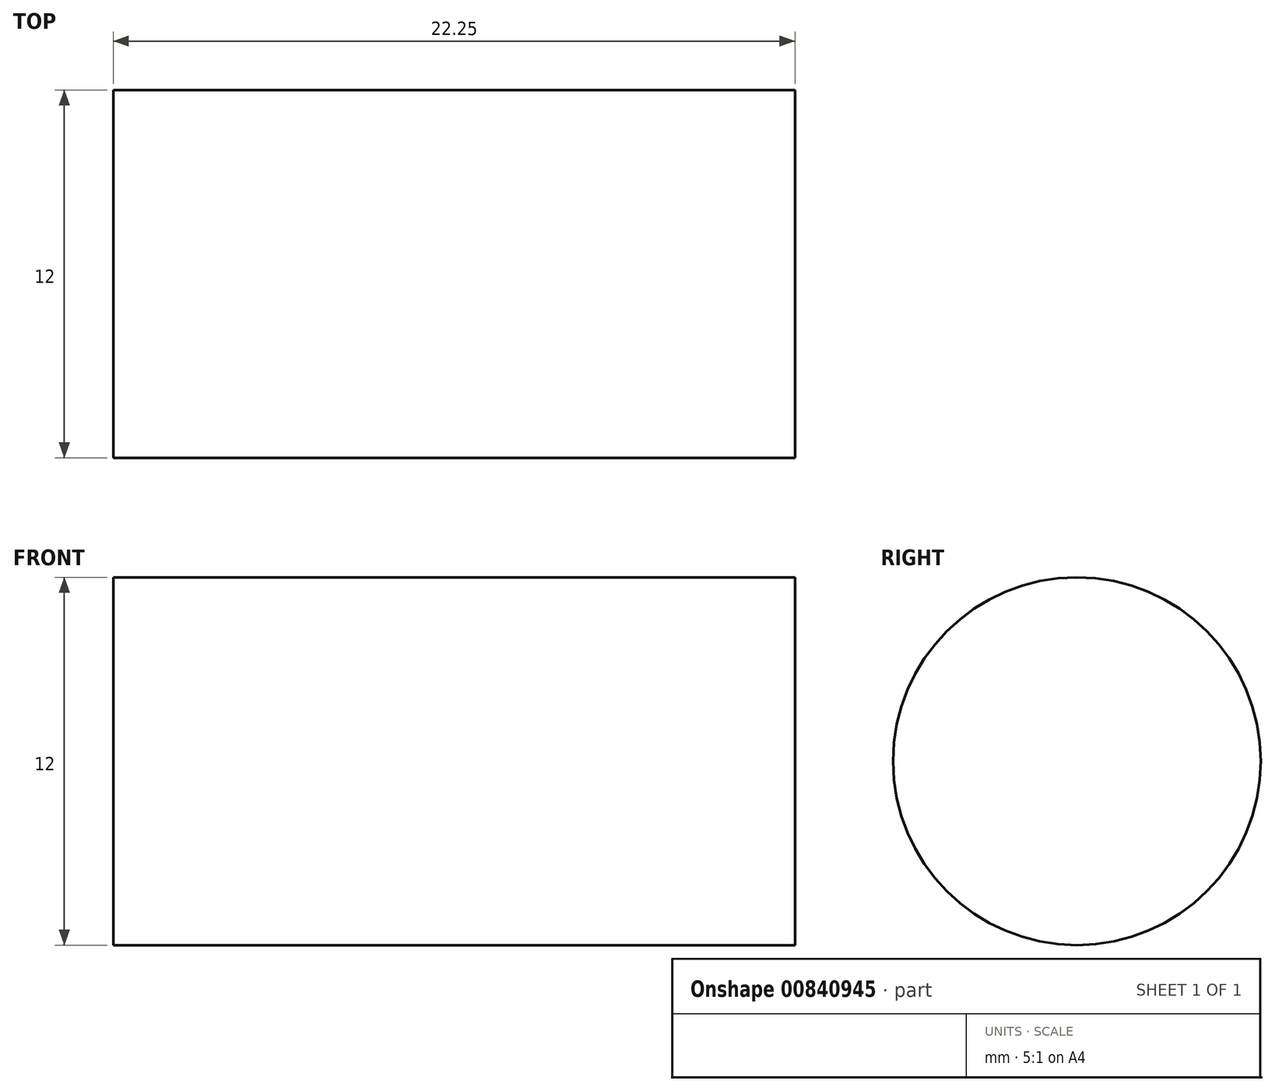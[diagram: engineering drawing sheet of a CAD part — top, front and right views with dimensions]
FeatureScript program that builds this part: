
annotation { "Feature Type Name" : "Feature", "Feature Type Description" : "" }
export const myFeature = defineFeature(function(context is Context, id is Id, definition is map)
    precondition{}
    {
        {
            var Q0;
            Q0=qCreatedBy(makeId("Right.planeOp"),FACE);
            var sketch = newSketch(context, id + "F0", { "sketchPlane" : qUnion([Q0])});
            skCircle(sketch, "E0", {"center": v(0, 0) * mm, "radius": 6 * mm});
            skSolve(sketch);
        }
        {
            var Q0;
            Q0 = qSketchRegion(id + "F0", true);
            extrude(context, id + "F1", {"entities" : qUnion([Q0]), "depth" : 22.25 * mm, "offsetDistance" : 25 * mm});
        }
    });
